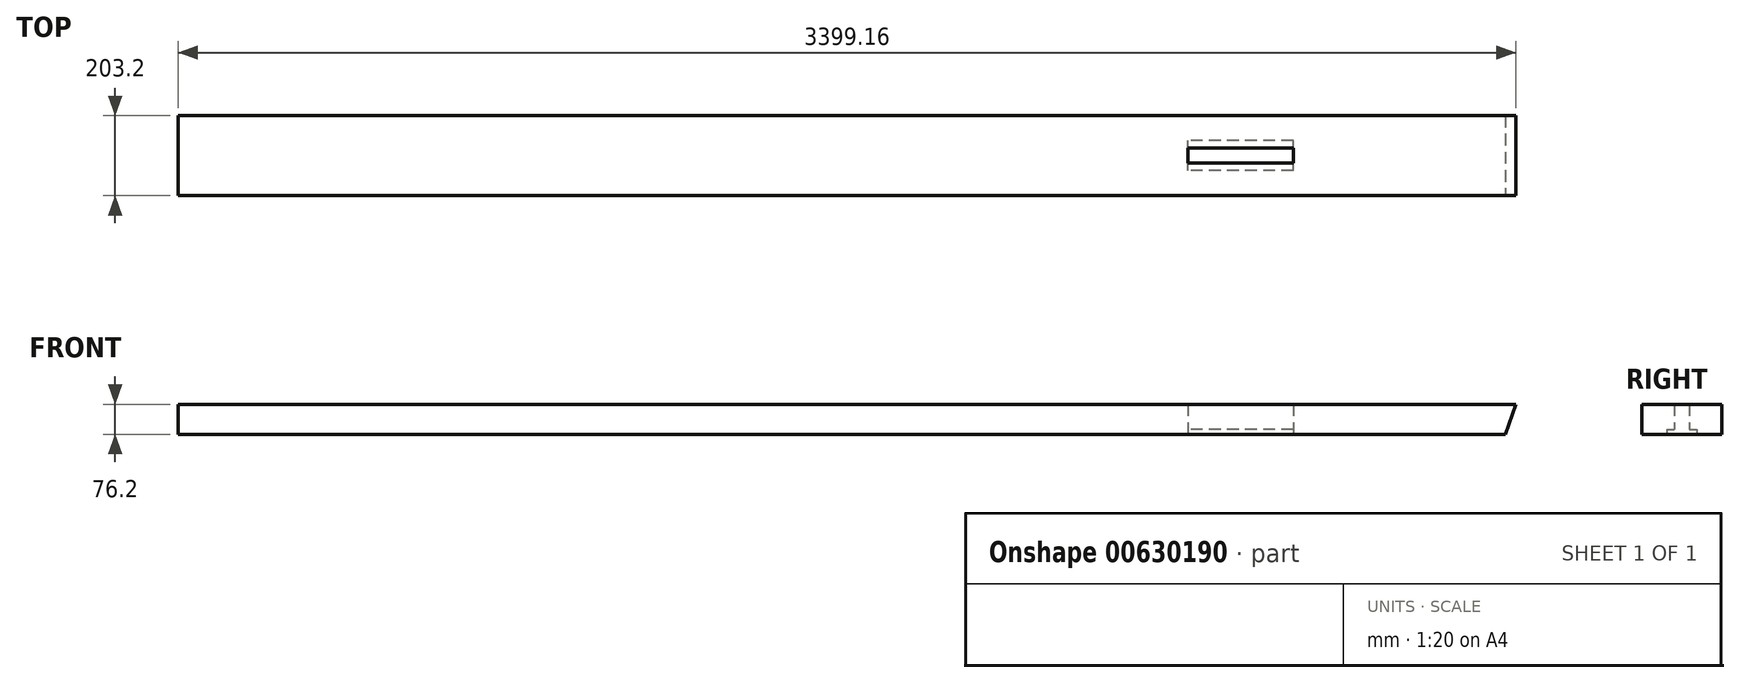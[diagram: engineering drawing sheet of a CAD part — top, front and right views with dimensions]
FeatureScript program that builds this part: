
annotation { "Feature Type Name" : "Feature", "Feature Type Description" : "" }
export const myFeature = defineFeature(function(context is Context, id is Id, definition is map)
    precondition{}
    {
        {
            var Q0;
            Q0=qCreatedBy(makeId("Front.planeOp"),FACE);
            var sketch = newSketch(context, id + "F0", { "sketchPlane" : qUnion([Q0])});
            skLineSegment(sketch, "E0.bottom", {"start": v(-1699.58, 38.1) * mm, "end": v(1699.58, 38.1) * mm});
            skLineSegment(sketch, "E0.top", {"start": v(-1699.58, -38.1) * mm, "end": v(1699.58, -38.1) * mm});
            skLineSegment(sketch, "E0.left", {"start": v(-1699.58, 38.1) * mm, "end": v(-1699.58, -38.1) * mm});
            skLineSegment(sketch, "E0.right", {"start": v(1699.58, 38.1) * mm, "end": v(1699.58, -38.1) * mm});
            skPoint(sketch, "E0.middle", {"position": v(0, 0) * mm});
            skSolve(sketch);
        }
        {
            var Q0;
            Q0 = qSketchRegion(id + "F0", true);
            extrude(context, id + "F1", {"entities" : qUnion([Q0]), "depth" : 203.2 * mm, "offsetDistance" : 25.4 * mm});
        }
        {
            var Q0;
            Q0=makeQuery(id+"F1.opExtrude","CAP_FACE",FACE,{"disambiguationData":[OSD([sQuery(id+"F0.wireOp",EDGE,"E0.bottom"),sQuery(id+"F0.wireOp",EDGE,"E0.top"),sQuery(id+"F0.wireOp",EDGE,"E0.left"),sQuery(id+"F0.wireOp",EDGE,"E0.right")])],"isStart":false});
            var sketch = newSketch(context, id + "F2", { "sketchPlane" : qUnion([Q0])});
            skLineSegment(sketch, "E1", {"start": v(1699.58, 38.1) * mm, "end": v(1671.9, -38.1) * mm});
            skSolve(sketch);
        }
        {
            var Q0;
            {var subQ0=sQuery(id+"F2.wireOp",EDGE,"E1");Q0=makeQuery(id+"F2.imprint","IMPRINT",FACE,{"disambiguationData":[TD([[makeQuery(id+"F2.imprint","IMPRINT",EDGE,{"derivedFrom":subQ0}),1.0]])]});}
            extrude(context, id + "F3", {"entities" : qUnion([Q0]), "operationType" : NewBodyOperationType.REMOVE, "oppositeDirection" : true, "depth" : 203.2 * mm, "offsetDistance" : 25.4 * mm});
        }
        {
            var Q0;
            Q0=makeQuery(id+"F1.opExtrude","SWEPT_FACE",FACE,{"disambiguationData":[OSD([sQuery(id+"F0.wireOp",EDGE,"E0.top")])]});
            var sketch = newSketch(context, id + "F4", { "sketchPlane" : qUnion([Q0])});
            skLineSegment(sketch, "E2.bottom", {"start": v(1133.25, 139.7) * mm, "end": v(866.02, 139.7) * mm});
            skLineSegment(sketch, "E2.top", {"start": v(1133.25, 63.5) * mm, "end": v(866.02, 63.5) * mm});
            skLineSegment(sketch, "E2.left", {"start": v(1133.25, 139.7) * mm, "end": v(1133.25, 63.5) * mm});
            skLineSegment(sketch, "E2.right", {"start": v(866.02, 139.7) * mm, "end": v(866.02, 63.5) * mm});
            skLineSegment(sketch, "E3.bottom", {"start": v(1133.25, 120.65) * mm, "end": v(866.02, 120.65) * mm});
            skLineSegment(sketch, "E3.top", {"start": v(1133.25, 82.55) * mm, "end": v(866.02, 82.55) * mm});
            skLineSegment(sketch, "E3.left", {"start": v(1133.25, 120.65) * mm, "end": v(1133.25, 82.55) * mm});
            skLineSegment(sketch, "E3.right", {"start": v(866.02, 120.65) * mm, "end": v(866.02, 82.55) * mm});
            skSolve(sketch);
        }
        {
            var Q0;
            Q0=makeQuery(id+"F4.imprint","IMPRINT",FACE,{"disambiguationData":[TD([[makeQuery(id+"F4.imprint","IMPRINT",EDGE,{"derivedFrom":sQuery(id+"F4.wireOp",EDGE,"E3.bottom")}),1.0]])]});
            extrude(context, id + "F5", {"entities" : qUnion([Q0]), "operationType" : NewBodyOperationType.REMOVE, "oppositeDirection" : true, "depth" : 76.2 * mm, "offsetDistance" : 25.4 * mm});
        }
        {
            var Q0;
            {var subQ0=sQuery(id+"F4.wireOp",EDGE,"E2.bottom");Q0=makeQuery(id+"F4.imprint","IMPRINT",FACE,{"disambiguationData":[TD([[makeQuery(id+"F4.imprint","IMPRINT",EDGE,{"derivedFrom":subQ0}),1.0]])]});}
            var Q1;
            {var subQ0=sQuery(id+"F4.wireOp",EDGE,"E2.top");Q1=makeQuery(id+"F4.imprint","IMPRINT",FACE,{"disambiguationData":[TD([[makeQuery(id+"F4.imprint","IMPRINT",EDGE,{"derivedFrom":subQ0}),-1.0]])]});}
            extrude(context, id + "F6", {"entities" : qUnion([Q0, Q1]), "operationType" : NewBodyOperationType.REMOVE, "oppositeDirection" : true, "depth" : 12.7 * mm, "offsetDistance" : 25.4 * mm});
        }
    });
